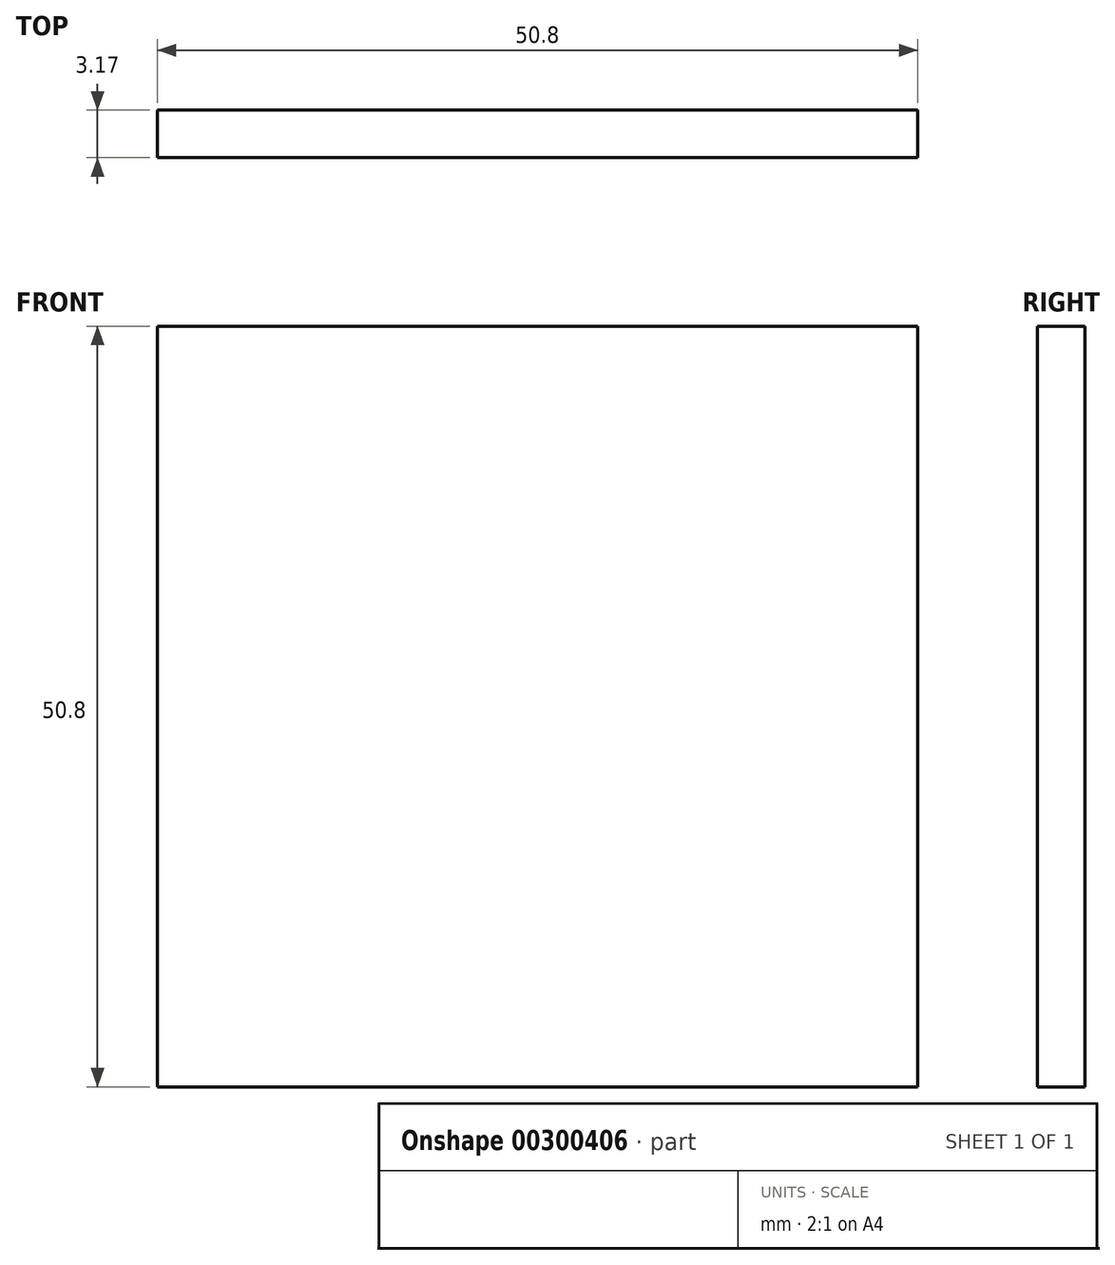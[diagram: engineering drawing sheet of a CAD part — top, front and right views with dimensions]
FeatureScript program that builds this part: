
annotation { "Feature Type Name" : "Feature", "Feature Type Description" : "" }
export const myFeature = defineFeature(function(context is Context, id is Id, definition is map)
    precondition{}
    {
        {
            var Q0;
            Q0=qCreatedBy(makeId("Front.planeOp"),FACE);
            var sketch = newSketch(context, id + "F0", { "sketchPlane" : qUnion([Q0])});
            skLineSegment(sketch, "E0.bottom", {"start": v(25.4, 25.4) * mm, "end": v(-25.4, 25.4) * mm});
            skLineSegment(sketch, "E0.top", {"start": v(25.4, -25.4) * mm, "end": v(-25.4, -25.4) * mm});
            skLineSegment(sketch, "E0.left", {"start": v(25.4, 25.4) * mm, "end": v(25.4, -25.4) * mm});
            skLineSegment(sketch, "E0.right", {"start": v(-25.4, 25.4) * mm, "end": v(-25.4, -25.4) * mm});
            skPoint(sketch, "E0.middle", {"position": v(0, 0) * mm});
            skSolve(sketch);
        }
        {
            var Q0;
            Q0 = qSketchRegion(id + "F0", true);
            extrude(context, id + "F1", {"entities" : qUnion([Q0]), "depth" : 3.17 * mm});
        }
    });
